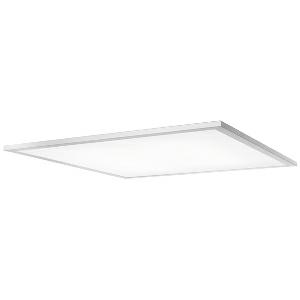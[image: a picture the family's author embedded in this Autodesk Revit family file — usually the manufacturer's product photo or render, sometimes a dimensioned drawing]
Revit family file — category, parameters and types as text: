
# Revit family: dotoo_fit_-_dfe_4000_830_d_sm600_00808120_9a87
name_source: partatom
category: Lighting Fixtures
units: mm (PartAtom-declared; Revit-internal decimal feet)

## family parameters
Cut with Voids When Loaded = No
Host = Face
Light Source = No
Part Type = Normal
Room Calculation Point = No
Round Connector Dimension = Use Diameter
Shared = No

## types (1)
- DOTOO.fit - DFE 4000/830/D SM600 (1 x LED, 3900 lm, 4000K)
    Apparent Load = 30 VA
    Approval mark = CE
    CIE Flux Codes = 66 90 98 100 100
    Color Rendering = 80-89
    Color Temperature = 4000K
    Control Gear = Electronic ballast
    Default Elevation = 1800 mm
    Description = DFE 4000/830/D|Recessed modular luminaire|light source:  |work equipment: Electronic ballast|connected load: 220-240V, 50/60Hz|Power consumption: approx. 30 W|standby: approx. 0,50|power factor: approx. 0,900|luminous flux: 3900 lm|luminous efficacy: 130 lm/W|light distribution: Direct|direct ratio: approx. 100 %|colour temperature: Warm white, ca. 3000 K|color rendering index (CRI): >= 80|chromaticity tolerance:  3 SDCM|System of protection: IP 20|class of protection: II|technology: Continuously dimmable|operation: External|luminaire body|material: Sectional aluminium|colour: White|weight (net): approx. 2.9 kg|mains lead: 0.50 m Connector|glare control: Prism aperture|luminance(L65): <= 2600 cd/m|unified glare rating(4H 8H): <=  19|special features: DALI Load 1x, TouchDIM - dimming via standard switch, Direct light component with edge light and light-guide technology for homogenous light exit, Flicker-free, System dimension 600 x 600 mm, Strain relief with the possibility of through-wiring|
    Height = 0 mm  [stored 0 ft]
    Lamp = 1 x LED
    Lamp Light Flux = 3900 lm
    Lamp count = 1
    Length = 596 mm
    Luminous efficacy = 130 lm/W
    Manufacturer = Waldmann
    ModVariant = No
    Model = 00808120
    Mounting Place = Ceiling
    Mounting Type = Recessed
    Number of Poles = 1
    OnlyDefault = Yes
    Power Factor = 1
    Product Name = DOTOO.fit - DFE 4000/830/D SM600
    Product group = Recessed luminaire
    ProductGroupID = 4
    Protection Class = Protection class II
    Protection Degree = IP 20
    RLX_Detail_Level = 1
    RLX_Emergency_Light_Flux = 0 lm
    RLX_Emergency_Type = 0
    RLX_Emergency_Type_DB = No
    RlxData = <blob elided: 37693 chars, md5=a5876e9b>
    Socket = socket
    Standby Power = 0 W
    System Light Flux = 3900 lm
    System Power = 30 W
    Type Comments = Product without accessories
    Type Image = 113328000-00692486.jpg
    URL = http://relux.com
    VarID = ---
    Voltage = 230 V
    Voltage Range = 220-240 V
    Weight = 0.00 kg
    Width = 596 mm

note: [stored X ft] marks values corroborated as IEEE doubles in the binary element streams (Revit-internal decimal feet)

## geometry (parser evidence)
native form markers: Blend x4, Sweep x9
no freeform markers — native parametric forms only
